# Revit family: GS50
name_source: partatom
category: Generic Models
units: mm (PartAtom-declared; Revit-internal decimal feet)

## family parameters
Always vertical = Yes
Can host rebar = No
Cut with Voids When Loaded = No
Part Type = Normal
Room Calculation Point = No
Round Connector Dimension = Use Diameter
Shared = Yes
Work Plane-Based = No

## types (2) — shared parameters
Model = GS50°
Type Comments = Neiging 50° tot 66°
afstand trapboom01 = 154 mm  [stored 0.505249 ft]
lengte trapboom-02 = 3300 mm  [stored 10.8268 ft]
vaste trap = gietaluminium

## per-type parameters (varying)
| type | URL | hoogte montagebeugel | hoogte onderste_bovenste treden | lengte trapboom-01 | trapschuinte |
| GS50_50gr | https://www.gortergroup.com | 2319 mm | 2500 mm  [stored 8.2021 ft] | 3300 mm  [stored 10.8268 ft] | 50.00° |
| GS50_66gr |  | 2819 mm  [stored 9.24869 ft] | 3000 mm  [stored 9.84252 ft] | 3150 mm  [stored 10.3346 ft] | 66.00° |

note: [stored X ft] marks values corroborated as IEEE doubles in the binary element streams (Revit-internal decimal feet)

## geometry (parser evidence)
native form markers: Sweep x8
no freeform markers — native parametric forms only
